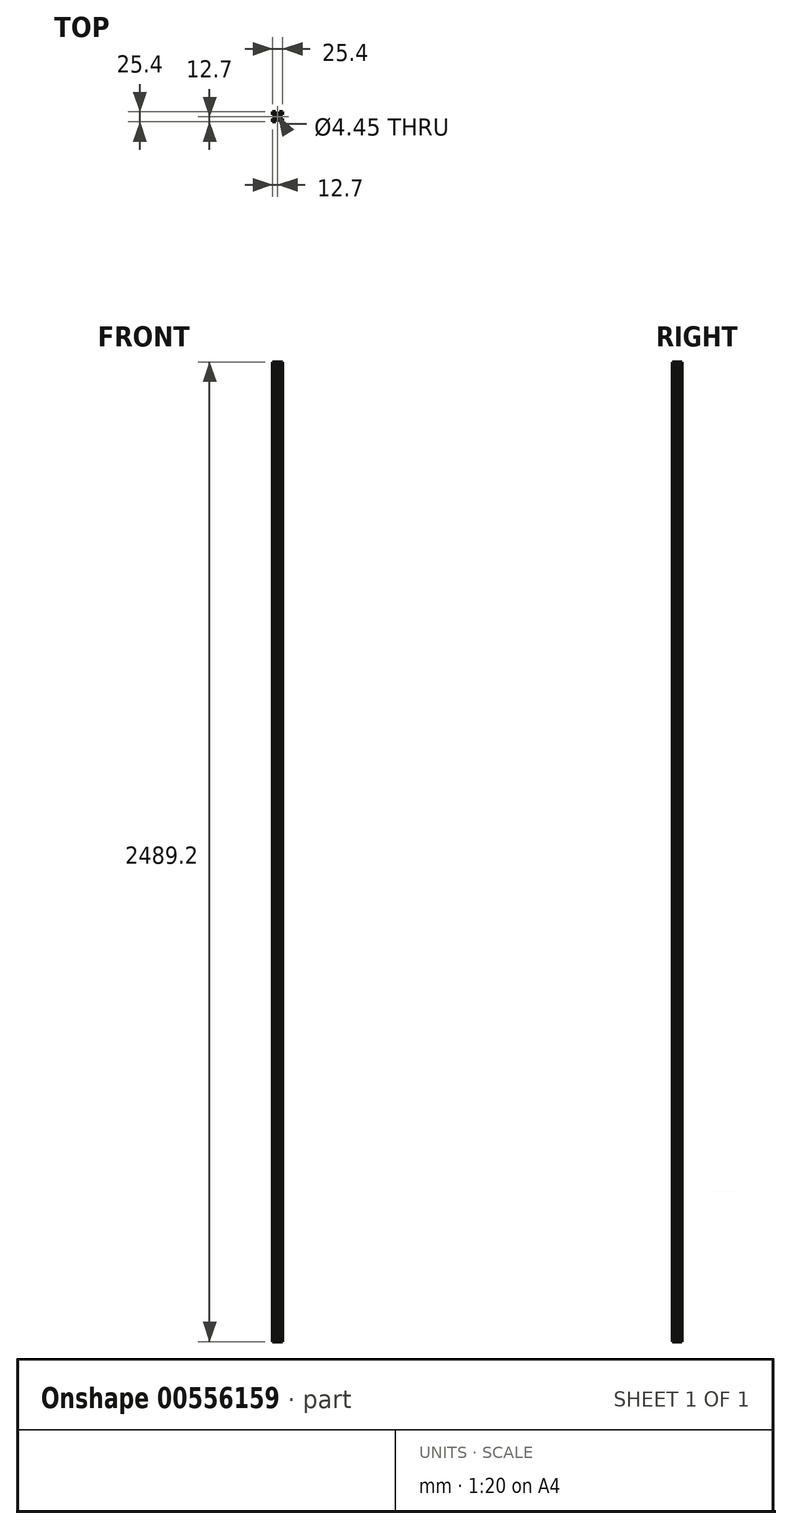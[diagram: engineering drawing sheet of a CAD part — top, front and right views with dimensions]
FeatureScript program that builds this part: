
annotation { "Feature Type Name" : "Feature", "Feature Type Description" : "" }
export const myFeature = defineFeature(function(context is Context, id is Id, definition is map)
    precondition{}
    {
        {
            var Q0;
            Q0=qCreatedBy(makeId("Top.planeOp"),FACE);
            var sketch = newSketch(context, id + "F0", { "sketchPlane" : qUnion([Q0])});
            skLineSegment(sketch, "E0.bottom", {"start": v(0, 0) * mm, "end": v(25.4, 0) * mm});
            skLineSegment(sketch, "E0.top", {"start": v(0, -25.4) * mm, "end": v(25.4, -25.4) * mm});
            skLineSegment(sketch, "E0.left", {"start": v(0, 0) * mm, "end": v(0, -25.4) * mm});
            skLineSegment(sketch, "E0.right", {"start": v(25.4, 0) * mm, "end": v(25.4, -25.4) * mm});
            skPoint(sketch, "E1.endSnap0", {"position": v(12.7, 0) * mm});
            skSolve(sketch);
        }
        {
            var Q0;
            Q0=makeQuery(id+"F0.imprint","IMPRINT",FACE,{"disambiguationData":[TD([[makeQuery(id+"F0.imprint","IMPRINT",EDGE,{"derivedFrom":sQuery(id+"F0.wireOp",EDGE,"E0.bottom")}),-1.0]])]});
            extrude(context, id + "F1", {"entities" : qUnion([Q0]), "depth" : 2489.2 * mm, "offsetDistance" : 25.4 * mm});
        }
        {
            var Q0;
            Q0=makeQuery(id+"F1.opExtrude","CAP_FACE",FACE,{"disambiguationData":[OSD([sQuery(id+"F0.wireOp",EDGE,"E0.bottom"),sQuery(id+"F0.wireOp",EDGE,"E0.top"),sQuery(id+"F0.wireOp",EDGE,"E0.left"),sQuery(id+"F0.wireOp",EDGE,"E0.right")])],"isStart":true});
            var sketch = newSketch(context, id + "F2", { "sketchPlane" : qUnion([Q0])});
            skLineSegment(sketch, "E2", {"start": v(0, 25.4) * mm, "end": v(7.62, 25.4) * mm});
            skLineSegment(sketch, "E3", {"start": v(0, 25.4) * mm, "end": v(0, 17.78) * mm});
            skLineSegment(sketch, "E4", {"start": v(0, 17.78) * mm, "end": v(2.54, 17.78) * mm});
            skLineSegment(sketch, "E5", {"start": v(7.62, 25.4) * mm, "end": v(7.62, 22.86) * mm});
            skLineSegment(sketch, "E6", {"start": v(7.62, 22.86) * mm, "end": v(2.54, 22.86) * mm});
            skLineSegment(sketch, "E7", {"start": v(2.54, 22.86) * mm, "end": v(2.54, 17.78) * mm});
            skLineSegment(sketch, "E8.MirrorCS", {"start": v(25.4, 17.78) * mm, "end": v(22.86, 17.78) * mm});
            skLineSegment(sketch, "E9.MirrorCS", {"start": v(25.4, 25.4) * mm, "end": v(17.78, 25.4) * mm});
            skLineSegment(sketch, "E10.MirrorCS", {"start": v(25.4, 25.4) * mm, "end": v(25.4, 17.78) * mm});
            skLineSegment(sketch, "E11.MirrorCS", {"start": v(17.78, 22.86) * mm, "end": v(22.86, 22.86) * mm});
            skLineSegment(sketch, "E12.MirrorCS", {"start": v(17.78, 25.4) * mm, "end": v(17.78, 22.86) * mm});
            skLineSegment(sketch, "E13.MirrorCS", {"start": v(22.86, 22.86) * mm, "end": v(22.86, 17.78) * mm});
            skLineSegment(sketch, "E14.MirrorCS", {"start": v(22.86, 2.54) * mm, "end": v(22.86, 7.62) * mm});
            skLineSegment(sketch, "E15.MirrorCS", {"start": v(17.78, 0) * mm, "end": v(17.78, 2.54) * mm});
            skLineSegment(sketch, "E16.MirrorCS", {"start": v(7.62, 2.54) * mm, "end": v(2.54, 2.54) * mm});
            skLineSegment(sketch, "E17.MirrorCS", {"start": v(25.4, 7.62) * mm, "end": v(22.86, 7.62) * mm});
            skLineSegment(sketch, "E18.MirrorCS", {"start": v(0, 7.62) * mm, "end": v(2.54, 7.62) * mm});
            skLineSegment(sketch, "E19.MirrorCS", {"start": v(7.62, 0) * mm, "end": v(7.62, 2.54) * mm});
            skLineSegment(sketch, "E20.MirrorCS", {"start": v(25.4, 0) * mm, "end": v(25.4, 7.62) * mm});
            skLineSegment(sketch, "E21.MirrorCS", {"start": v(17.78, 2.54) * mm, "end": v(22.86, 2.54) * mm});
            skLineSegment(sketch, "E22.MirrorCS", {"start": v(25.4, 0) * mm, "end": v(17.78, 0) * mm});
            skLineSegment(sketch, "E23.MirrorCS", {"start": v(0, 0) * mm, "end": v(0, 7.62) * mm});
            skLineSegment(sketch, "E24.MirrorCS", {"start": v(0, 0) * mm, "end": v(7.62, 0) * mm});
            skLineSegment(sketch, "E25.MirrorCS", {"start": v(2.54, 2.54) * mm, "end": v(2.54, 7.62) * mm});
            skLineSegment(sketch, "E26", {"start": v(12.7, 16.51) * mm, "end": v(16.51, 16.51) * mm});
            skLineSegment(sketch, "E27.bottom", {"start": v(16.51, 16.51) * mm, "end": v(8.9, 16.51) * mm});
            skLineSegment(sketch, "E27.top", {"start": v(16.51, 8.9) * mm, "end": v(8.9, 8.9) * mm});
            skLineSegment(sketch, "E27.left", {"start": v(16.51, 16.51) * mm, "end": v(16.51, 8.9) * mm});
            skLineSegment(sketch, "E27.right", {"start": v(8.9, 16.51) * mm, "end": v(8.9, 8.9) * mm});
            skPoint(sketch, "E28.orphan", {"position": v(25.4, 12.7) * mm});
            skPoint(sketch, "E29.orphan", {"position": v(0, 12.7) * mm});
            skPoint(sketch, "E30.orphan", {"position": v(12.7, 25.4) * mm});
            skPoint(sketch, "E31.orphan", {"position": v(12.7, 0) * mm});
            skPoint(sketch, "E32.orphan", {"position": v(2.4, 24.8) * mm});
            skPoint(sketch, "E33.orphan", {"position": v(0.6, 23) * mm});
            skPoint(sketch, "E34.orphan", {"position": v(0.6, 2.4) * mm});
            skPoint(sketch, "E35.orphan", {"position": v(2.4, 0.6) * mm});
            skLineSegment(sketch, "E36.trimOffspring", {"start": v(8.9, 10.69) * mm, "end": v(2.54, 4.34) * mm});
            skLineSegment(sketch, "E37.trimOffspring", {"start": v(10.69, 8.9) * mm, "end": v(4.34, 2.54) * mm});
            skLineSegment(sketch, "E38.trimOffspring", {"start": v(8.9, 14.71) * mm, "end": v(2.54, 21.06) * mm});
            skLineSegment(sketch, "E39.trimOffspring", {"start": v(10.69, 16.51) * mm, "end": v(4.34, 22.86) * mm});
            skLineSegment(sketch, "E40.trimOffspring", {"start": v(14.71, 16.51) * mm, "end": v(21.06, 22.86) * mm});
            skLineSegment(sketch, "E41.trimOffspring", {"start": v(16.51, 14.71) * mm, "end": v(22.86, 21.06) * mm});
            skLineSegment(sketch, "E42.trimOffspring", {"start": v(16.5, 10.69) * mm, "end": v(22.86, 4.34) * mm});
            skLineSegment(sketch, "E43.trimOffspring", {"start": v(14.71, 8.9) * mm, "end": v(21.06, 2.54) * mm});
            skPoint(sketch, "E44.orphan", {"position": v(23, 0.6) * mm});
            skPoint(sketch, "E45.orphan", {"position": v(24.8, 2.4) * mm});
            skPoint(sketch, "E46.orphan", {"position": v(24.8, 23) * mm});
            skPoint(sketch, "E47.orphan", {"position": v(23, 24.8) * mm});
            skCircle(sketch, "E48", {"center": v(12.7, 12.7) * mm, "radius": 2.22 * mm});
            skSolve(sketch);
        }
        {
            var Q0;
            {var subQ4=sQuery(id+"F2.wireOp",EDGE,"E4");Q0=makeQuery(id+"F2.imprint","IMPRINT",FACE,{"disambiguationData":[TD([[makeQuery(id+"F2.imprint","IMPRINT",EDGE,{"derivedFrom":subQ4}),-1.0]])]});}
            var Q1;
            {var subQ1=sQuery(id+"F2.wireOp",EDGE,"E15.MirrorCS");Q1=makeQuery(id+"F2.imprint","IMPRINT",FACE,{"disambiguationData":[TD([[makeQuery(id+"F2.imprint","IMPRINT",EDGE,{"derivedFrom":subQ1}),1.0]])]});}
            var Q2;
            {var subQ5=sQuery(id+"F2.wireOp",EDGE,"E8.MirrorCS");Q2=makeQuery(id+"F2.imprint","IMPRINT",FACE,{"disambiguationData":[TD([[makeQuery(id+"F2.imprint","IMPRINT",EDGE,{"derivedFrom":subQ5}),1.0]])]});}
            var Q3;
            {var subQ1=sQuery(id+"F2.wireOp",EDGE,"E5");Q3=makeQuery(id+"F2.imprint","IMPRINT",FACE,{"disambiguationData":[TD([[makeQuery(id+"F2.imprint","IMPRINT",EDGE,{"derivedFrom":subQ1}),1.0]])]});}
            extrude(context, id + "F3", {"entities" : qUnion([Q0, Q1, Q2, Q3]), "operationType" : NewBodyOperationType.REMOVE, "oppositeDirection" : true, "depth" : 2489.2 * mm, "offsetDistance" : 25.4 * mm});
        }
        {
            var Q0;
            Q0=makeQuery(id+"F1.opExtrude","CAP_FACE",FACE,{"disambiguationData":[OSD([sQuery(id+"F0.wireOp",EDGE,"E0.bottom"),sQuery(id+"F0.wireOp",EDGE,"E0.top"),sQuery(id+"F0.wireOp",EDGE,"E0.left"),sQuery(id+"F0.wireOp",EDGE,"E0.right")])],"isStart":true});
            var sketch = newSketch(context, id + "F4", { "sketchPlane" : qUnion([Q0])});
            skCircle(sketch, "E49", {"center": v(12.7, 12.7) * mm, "radius": 2.22 * mm});
            skSolve(sketch);
        }
        {
            var Q0;
            Q0=makeQuery(id+"F4.imprint","IMPRINT",FACE,{"disambiguationData":[TD([[makeQuery(id+"F4.imprint","IMPRINT",EDGE,{"derivedFrom":sQuery(id+"F4.wireOp",EDGE,"E49")}),1.0]])]});
            extrude(context, id + "F5", {"entities" : qUnion([Q0]), "operationType" : NewBodyOperationType.REMOVE, "oppositeDirection" : true, "depth" : 2489.2 * mm, "offsetDistance" : 25.4 * mm});
        }
    });
